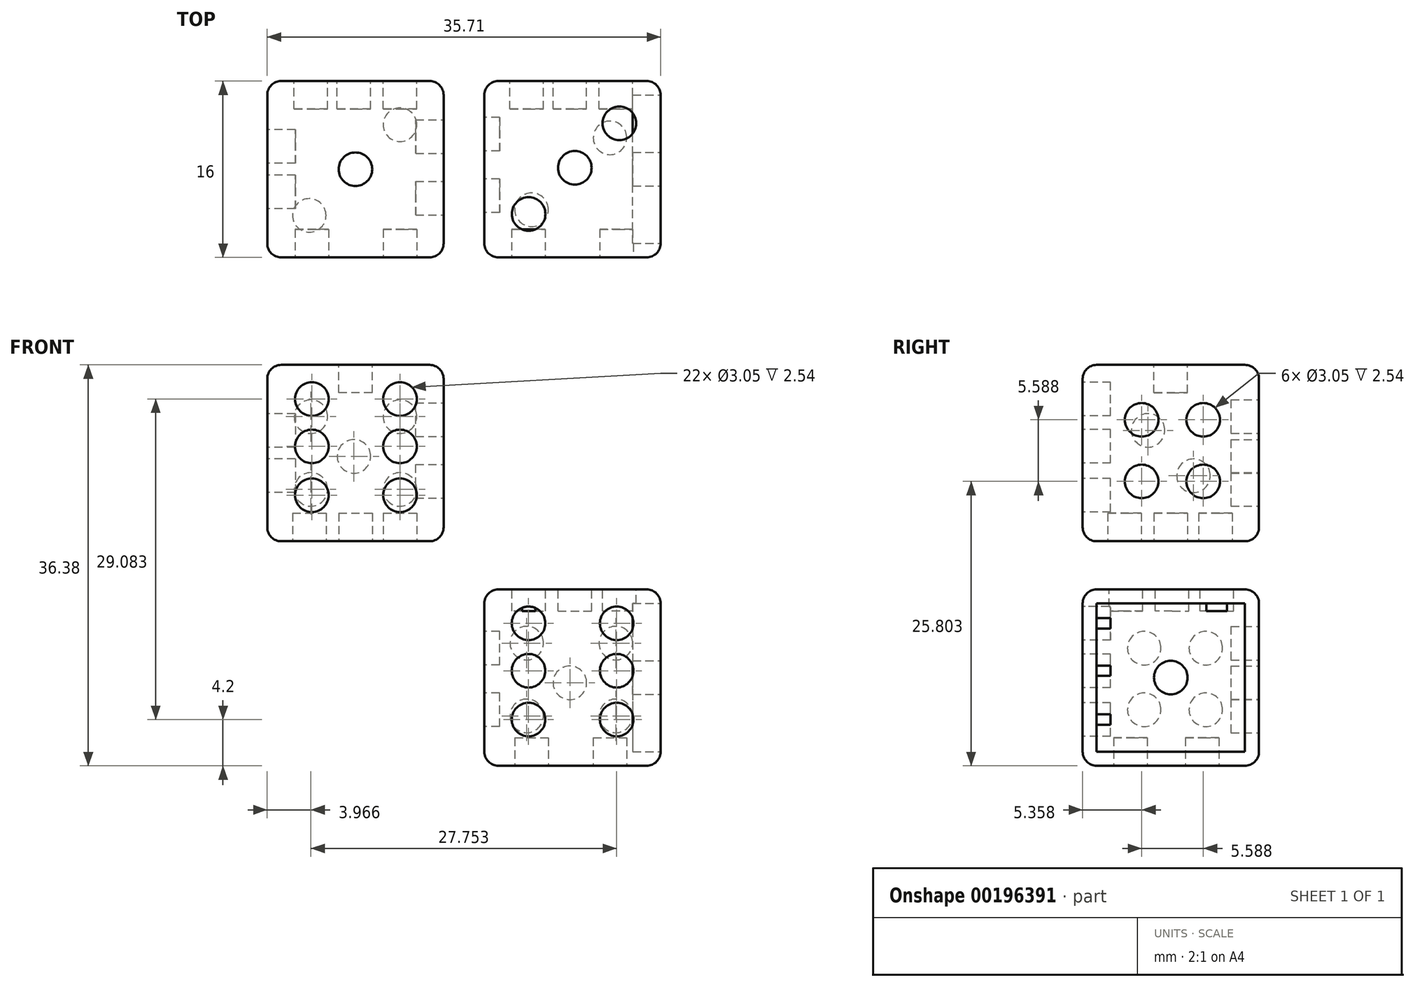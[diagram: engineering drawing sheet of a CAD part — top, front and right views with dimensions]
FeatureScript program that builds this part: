
annotation { "Feature Type Name" : "Feature", "Feature Type Description" : "" }
export const myFeature = defineFeature(function(context is Context, id is Id, definition is map)
    precondition{}
    {
        {
            var Q0;
            Q0=qCreatedBy(makeId("Front.planeOp"),FACE);
            var sketch = newSketch(context, id + "F0", { "sketchPlane" : qUnion([Q0])});
            skLineSegment(sketch, "E0.bottom", {"start": v(-12.05, 13.49) * mm, "end": v(3.96, 13.49) * mm});
            skLineSegment(sketch, "E0.top", {"start": v(-12.05, -2.52) * mm, "end": v(3.96, -2.52) * mm});
            skLineSegment(sketch, "E0.left", {"start": v(-12.05, 13.49) * mm, "end": v(-12.05, -2.52) * mm});
            skLineSegment(sketch, "E0.right", {"start": v(3.96, 13.49) * mm, "end": v(3.96, -2.52) * mm});
            skLineSegment(sketch, "E1.bottom", {"start": v(7.66, -6.89) * mm, "end": v(23.66, -6.89) * mm});
            skLineSegment(sketch, "E1.top", {"start": v(7.66, -22.89) * mm, "end": v(23.66, -22.89) * mm});
            skLineSegment(sketch, "E1.left", {"start": v(7.66, -6.89) * mm, "end": v(7.66, -22.89) * mm});
            skLineSegment(sketch, "E1.right", {"start": v(23.66, -6.89) * mm, "end": v(23.66, -22.89) * mm});
            skSolve(sketch);
        }
        {
            var Q0;
            Q0 = qSketchRegion(id + "F0", true);
            extrude(context, id + "F1", {"entities" : qUnion([Q0]), "depth" : 16 * mm});
        }
        {
            var Q0;
            Q0=makeQuery(id+"F1.opExtrude","SWEPT_EDGE",EDGE,{"disambiguationData":[OSD([sQuery(id+"F0.wireOp",EDGE,"E0.top"),sQuery(id+"F0.wireOp",EDGE,"E0.left")])]});
            var Q1;
            Q1=makeQuery(id+"F1.opExtrude","CAP_EDGE",EDGE,{"disambiguationData":[OSD([sQuery(id+"F0.wireOp",EDGE,"E0.top")])],"isStart":false});
            var Q2;
            Q2=makeQuery(id+"F1.opExtrude","CAP_EDGE",EDGE,{"disambiguationData":[OSD([sQuery(id+"F0.wireOp",EDGE,"E0.left")])],"isStart":false});
            var Q3;
            Q3=makeQuery(id+"F1.opExtrude","SWEPT_EDGE",EDGE,{"disambiguationData":[OSD([sQuery(id+"F0.wireOp",EDGE,"E0.top"),sQuery(id+"F0.wireOp",EDGE,"E0.right")])]});
            var Q4;
            Q4=makeQuery(id+"F1.opExtrude","CAP_EDGE",EDGE,{"disambiguationData":[OSD([sQuery(id+"F0.wireOp",EDGE,"E0.top")])],"isStart":true});
            var Q5;
            Q5=makeQuery(id+"F1.opExtrude","CAP_EDGE",EDGE,{"disambiguationData":[OSD([sQuery(id+"F0.wireOp",EDGE,"E0.left")])],"isStart":true});
            var Q6;
            Q6=makeQuery(id+"F1.opExtrude","CAP_EDGE",EDGE,{"disambiguationData":[OSD([sQuery(id+"F0.wireOp",EDGE,"E0.right")])],"isStart":true});
            var Q7;
            Q7=makeQuery(id+"F1.opExtrude","SWEPT_EDGE",EDGE,{"disambiguationData":[OSD([sQuery(id+"F0.wireOp",EDGE,"E0.bottom"),sQuery(id+"F0.wireOp",EDGE,"E0.right")])]});
            var Q8;
            Q8=makeQuery(id+"F1.opExtrude","CAP_EDGE",EDGE,{"disambiguationData":[OSD([sQuery(id+"F0.wireOp",EDGE,"E0.bottom")])],"isStart":false});
            var Q9;
            Q9=makeQuery(id+"F1.opExtrude","SWEPT_EDGE",EDGE,{"disambiguationData":[OSD([sQuery(id+"F0.wireOp",EDGE,"E0.bottom"),sQuery(id+"F0.wireOp",EDGE,"E0.left")])]});
            var Q10;
            Q10=makeQuery(id+"F1.opExtrude","CAP_EDGE",EDGE,{"disambiguationData":[OSD([sQuery(id+"F0.wireOp",EDGE,"E0.bottom")])],"isStart":true});
            var Q11;
            Q11=makeQuery(id+"F1.opExtrude","CAP_EDGE",EDGE,{"disambiguationData":[OSD([sQuery(id+"F0.wireOp",EDGE,"E0.right")])],"isStart":false});
            var Q12;
            Q12=makeQuery(id+"F1.opExtrude","CAP_EDGE",EDGE,{"disambiguationData":[OSD([sQuery(id+"F0.wireOp",EDGE,"E1.left")])],"isStart":false});
            var Q13;
            Q13=makeQuery(id+"F1.opExtrude","CAP_EDGE",EDGE,{"disambiguationData":[OSD([sQuery(id+"F0.wireOp",EDGE,"E1.right")])],"isStart":false});
            var Q14;
            Q14=makeQuery(id+"F1.opExtrude","CAP_EDGE",EDGE,{"disambiguationData":[OSD([sQuery(id+"F0.wireOp",EDGE,"E1.bottom")])],"isStart":false});
            var Q15;
            Q15=makeQuery(id+"F1.opExtrude","CAP_EDGE",EDGE,{"disambiguationData":[OSD([sQuery(id+"F0.wireOp",EDGE,"E1.top")])],"isStart":false});
            var Q16;
            Q16=makeQuery(id+"F1.opExtrude","SWEPT_FACE",FACE,{"disambiguationData":[OSD([sQuery(id+"F0.wireOp",EDGE,"E1.top")])]});
            var Q17;
            Q17=makeQuery(id+"F1.opExtrude","SWEPT_FACE",FACE,{"disambiguationData":[OSD([sQuery(id+"F0.wireOp",EDGE,"E1.left")])]});
            var Q18;
            Q18=makeQuery(id+"F1.opExtrude","CAP_FACE",FACE,{"disambiguationData":[OSD([sQuery(id+"F0.wireOp",EDGE,"E1.bottom"),sQuery(id+"F0.wireOp",EDGE,"E1.top"),sQuery(id+"F0.wireOp",EDGE,"E1.left"),sQuery(id+"F0.wireOp",EDGE,"E1.right")])],"isStart":true});
            var Q19;
            Q19=makeQuery(id+"F1.opExtrude","SWEPT_FACE",FACE,{"disambiguationData":[OSD([sQuery(id+"F0.wireOp",EDGE,"E1.right")])]});
            fillet(context, id + "F2", {"entities" : qUnion([Q0, Q1, Q2, Q3, Q4, Q5, Q6, Q7, Q8, Q9, Q10, Q11, Q12, Q13, Q14, Q15, Q16, Q17, Q18, Q19]), "radius" : 1.27 * mm, "tangentPropagation" : true, "allowEdgeOverflow" : false});
        }
        {
            var Q0;
            Q0=makeQuery(id+"F1.opExtrude","CAP_FACE",FACE,{"disambiguationData":[OSD([sQuery(id+"F0.wireOp",EDGE,"E0.bottom"),sQuery(id+"F0.wireOp",EDGE,"E0.top"),sQuery(id+"F0.wireOp",EDGE,"E0.left"),sQuery(id+"F0.wireOp",EDGE,"E0.right")])],"isStart":false});
            var sketch = newSketch(context, id + "F3", { "sketchPlane" : qUnion([Q0])});
            skPoint(sketch, "E2", {"position": v(-4.04, 12.22) * mm});
            skPoint(sketch, "E3", {"position": v(-4.04, -1.25) * mm});
            skPoint(sketch, "E4", {"position": v(-10.78, 5.49) * mm});
            skPoint(sketch, "E5", {"position": v(2.69, 5.49) * mm});
            skCircle(sketch, "E6", {"center": v(-8, 10.4) * mm, "radius": 1.52 * mm});
            skCircle(sketch, "E7", {"center": v(-8, 6.09) * mm, "radius": 1.52 * mm});
            skCircle(sketch, "E8", {"center": v(-8, 1.66) * mm, "radius": 1.52 * mm});
            skCircle(sketch, "E9", {"center": v(0, 10.4) * mm, "radius": 1.52 * mm});
            skCircle(sketch, "E10", {"center": v(0, 6.09) * mm, "radius": 1.52 * mm});
            skCircle(sketch, "E11", {"center": v(0, 1.66) * mm, "radius": 1.52 * mm});
            skPoint(sketch, "E12", {"position": v(15.62, -8.14) * mm});
            skPoint(sketch, "E13", {"position": v(15.62, -21.6) * mm});
            skPoint(sketch, "E14", {"position": v(8.9, -14.87) * mm});
            skPoint(sketch, "E15", {"position": v(22.36, -14.87) * mm});
            skCircle(sketch, "E16", {"center": v(11.67, -9.96) * mm, "radius": 1.52 * mm});
            skCircle(sketch, "E17", {"center": v(11.67, -14.27) * mm, "radius": 1.52 * mm});
            skCircle(sketch, "E18", {"center": v(11.67, -18.7) * mm, "radius": 1.52 * mm});
            skCircle(sketch, "E19", {"center": v(19.67, -9.96) * mm, "radius": 1.52 * mm});
            skCircle(sketch, "E20", {"center": v(19.67, -14.27) * mm, "radius": 1.52 * mm});
            skCircle(sketch, "E21", {"center": v(19.67, -18.7) * mm, "radius": 1.52 * mm});
            skSolve(sketch);
        }
        {
            var Q0;
            Q0=makeQuery(id+"F1.opExtrude","SWEPT_FACE",FACE,{"disambiguationData":[OSD([sQuery(id+"F0.wireOp",EDGE,"E0.right")])]});
            var sketch = newSketch(context, id + "F4", { "sketchPlane" : qUnion([Q0])});
            skCircle(sketch, "E22", {"center": v(-10.41, -12.22) * mm, "radius": 1.52 * mm});
            skCircle(sketch, "E23", {"center": v(-10.41, -17.8) * mm, "radius": 1.52 * mm});
            skCircle(sketch, "E24", {"center": v(-4.83, -12.22) * mm, "radius": 1.52 * mm});
            skCircle(sketch, "E25", {"center": v(-4.83, -17.8) * mm, "radius": 1.52 * mm});
            skCircle(sketch, "E26", {"center": v(-10.64, 8.5) * mm, "radius": 1.52 * mm});
            skCircle(sketch, "E27", {"center": v(-10.64, 2.91) * mm, "radius": 1.52 * mm});
            skCircle(sketch, "E28", {"center": v(-5.05, 8.5) * mm, "radius": 1.52 * mm});
            skCircle(sketch, "E29", {"center": v(-5.05, 2.91) * mm, "radius": 1.52 * mm});
            skSolve(sketch);
        }
        {
            var Q0;
            Q0=makeQuery(id+"F3.imprint","IMPRINT",FACE,{"disambiguationData":[TD([[makeQuery(id+"F3.imprint","IMPRINT",EDGE,{"derivedFrom":sQuery(id+"F3.wireOp",EDGE,"E10")}),1.0]])]});
            var Q1;
            Q1=makeQuery(id+"F3.imprint","IMPRINT",FACE,{"disambiguationData":[TD([[makeQuery(id+"F3.imprint","IMPRINT",EDGE,{"derivedFrom":sQuery(id+"F3.wireOp",EDGE,"E9")}),1.0]])]});
            var Q2;
            Q2=makeQuery(id+"F3.imprint","IMPRINT",FACE,{"disambiguationData":[TD([[makeQuery(id+"F3.imprint","IMPRINT",EDGE,{"derivedFrom":sQuery(id+"F3.wireOp",EDGE,"E6")}),1.0]])]});
            var Q3;
            Q3=makeQuery(id+"F3.imprint","IMPRINT",FACE,{"disambiguationData":[TD([[makeQuery(id+"F3.imprint","IMPRINT",EDGE,{"derivedFrom":sQuery(id+"F3.wireOp",EDGE,"E7")}),1.0]])]});
            var Q4;
            Q4=makeQuery(id+"F3.imprint","IMPRINT",FACE,{"disambiguationData":[TD([[makeQuery(id+"F3.imprint","IMPRINT",EDGE,{"derivedFrom":sQuery(id+"F3.wireOp",EDGE,"E8")}),1.0]])]});
            var Q5;
            Q5=makeQuery(id+"F3.imprint","IMPRINT",FACE,{"disambiguationData":[TD([[makeQuery(id+"F3.imprint","IMPRINT",EDGE,{"derivedFrom":sQuery(id+"F3.wireOp",EDGE,"E11")}),1.0]])]});
            extrude(context, id + "F5", {"entities" : qUnion([Q0, Q1, Q2, Q3, Q4, Q5]), "operationType" : NewBodyOperationType.REMOVE, "oppositeDirection" : true, "depth" : 2.54 * mm});
        }
        {
            var Q0;
            Q0=makeQuery(id+"F4.imprint","IMPRINT",FACE,{"disambiguationData":[TD([[makeQuery(id+"F4.imprint","IMPRINT",EDGE,{"derivedFrom":sQuery(id+"F4.wireOp",EDGE,"E22")}),1.0]])]});
            var Q1;
            Q1=makeQuery(id+"F4.imprint","IMPRINT",FACE,{"disambiguationData":[TD([[makeQuery(id+"F4.imprint","IMPRINT",EDGE,{"derivedFrom":sQuery(id+"F4.wireOp",EDGE,"E24")}),1.0]])]});
            var Q2;
            Q2=makeQuery(id+"F4.imprint","IMPRINT",FACE,{"disambiguationData":[TD([[makeQuery(id+"F4.imprint","IMPRINT",EDGE,{"derivedFrom":sQuery(id+"F4.wireOp",EDGE,"E23")}),1.0]])]});
            var Q3;
            Q3=makeQuery(id+"F4.imprint","IMPRINT",FACE,{"disambiguationData":[TD([[makeQuery(id+"F4.imprint","IMPRINT",EDGE,{"derivedFrom":sQuery(id+"F4.wireOp",EDGE,"E25")}),1.0]])]});
            extrude(context, id + "F6", {"entities" : qUnion([Q0, Q1, Q2, Q3]), "operationType" : NewBodyOperationType.REMOVE, "oppositeDirection" : true, "depth" : 3.8 * mm});
        }
        {
            var Q0;
            Q0=makeQuery(id+"F1.opExtrude","CAP_FACE",FACE,{"disambiguationData":[OSD([sQuery(id+"F0.wireOp",EDGE,"E0.bottom"),sQuery(id+"F0.wireOp",EDGE,"E0.top"),sQuery(id+"F0.wireOp",EDGE,"E0.left"),sQuery(id+"F0.wireOp",EDGE,"E0.right")])],"isStart":true});
            var sketch = newSketch(context, id + "F7", { "sketchPlane" : qUnion([Q0])});
            skCircle(sketch, "E30", {"center": v(0, 8.79) * mm, "radius": 1.52 * mm});
            skCircle(sketch, "E31", {"center": v(8.08, 8.79) * mm, "radius": 1.52 * mm});
            skCircle(sketch, "E32", {"center": v(0, 2.18) * mm, "radius": 1.52 * mm});
            skCircle(sketch, "E33", {"center": v(8.08, 2.18) * mm, "radius": 1.52 * mm});
            skCircle(sketch, "E34", {"center": v(4.18, 5.18) * mm, "radius": 1.52 * mm});
            skCircle(sketch, "E35", {"center": v(-19.6, -11.76) * mm, "radius": 1.52 * mm});
            skCircle(sketch, "E36", {"center": v(-11.5, -11.76) * mm, "radius": 1.52 * mm});
            skCircle(sketch, "E37", {"center": v(-19.6, -18.36) * mm, "radius": 1.52 * mm});
            skCircle(sketch, "E38", {"center": v(-11.5, -18.36) * mm, "radius": 1.52 * mm});
            skCircle(sketch, "E39", {"center": v(-15.42, -15.36) * mm, "radius": 1.52 * mm});
            skSolve(sketch);
        }
        {
            var Q0;
            Q0=makeQuery(id+"F7.imprint","IMPRINT",FACE,{"disambiguationData":[TD([[makeQuery(id+"F7.imprint","IMPRINT",EDGE,{"derivedFrom":sQuery(id+"F7.wireOp",EDGE,"E30")}),1.0]])]});
            var Q1;
            Q1=makeQuery(id+"F7.imprint","IMPRINT",FACE,{"disambiguationData":[TD([[makeQuery(id+"F7.imprint","IMPRINT",EDGE,{"derivedFrom":sQuery(id+"F7.wireOp",EDGE,"E34")}),1.0]])]});
            var Q2;
            Q2=makeQuery(id+"F7.imprint","IMPRINT",FACE,{"disambiguationData":[TD([[makeQuery(id+"F7.imprint","IMPRINT",EDGE,{"derivedFrom":sQuery(id+"F7.wireOp",EDGE,"E31")}),1.0]])]});
            var Q3;
            Q3=makeQuery(id+"F7.imprint","IMPRINT",FACE,{"disambiguationData":[TD([[makeQuery(id+"F7.imprint","IMPRINT",EDGE,{"derivedFrom":sQuery(id+"F7.wireOp",EDGE,"E32")}),1.0]])]});
            var Q4;
            Q4=makeQuery(id+"F7.imprint","IMPRINT",FACE,{"disambiguationData":[TD([[makeQuery(id+"F7.imprint","IMPRINT",EDGE,{"derivedFrom":sQuery(id+"F7.wireOp",EDGE,"E33")}),1.0]])]});
            extrude(context, id + "F8", {"entities" : qUnion([Q0, Q1, Q2, Q3, Q4]), "operationType" : NewBodyOperationType.REMOVE, "oppositeDirection" : true, "depth" : 2.54 * mm});
        }
        {
            var Q0;
            Q0=makeQuery(id+"F1.opExtrude","SWEPT_FACE",FACE,{"disambiguationData":[OSD([sQuery(id+"F0.wireOp",EDGE,"E0.top")])]});
            var sketch = newSketch(context, id + "F9", { "sketchPlane" : qUnion([Q0])});
            skCircle(sketch, "E40", {"center": v(-8.24, 12.2) * mm, "radius": 1.52 * mm});
            skCircle(sketch, "E41", {"center": v(-4.04, 8) * mm, "radius": 1.52 * mm});
            skCircle(sketch, "E42", {"center": v(0, 3.96) * mm, "radius": 1.52 * mm});
            skCircle(sketch, "E43", {"center": v(11.68, 12.06) * mm, "radius": 1.52 * mm});
            skCircle(sketch, "E44", {"center": v(15.87, 7.87) * mm, "radius": 1.52 * mm});
            skCircle(sketch, "E45", {"center": v(19.91, 3.83) * mm, "radius": 1.52 * mm});
            skSolve(sketch);
        }
        {
            var Q0;
            Q0=makeQuery(id+"F9.imprint","IMPRINT",FACE,{"disambiguationData":[TD([[makeQuery(id+"F9.imprint","IMPRINT",EDGE,{"derivedFrom":sQuery(id+"F9.wireOp",EDGE,"E40")}),1.0]])]});
            var Q1;
            Q1=makeQuery(id+"F9.imprint","IMPRINT",FACE,{"disambiguationData":[TD([[makeQuery(id+"F9.imprint","IMPRINT",EDGE,{"derivedFrom":sQuery(id+"F9.wireOp",EDGE,"E42")}),1.0]])]});
            var Q2;
            Q2=makeQuery(id+"F9.imprint","IMPRINT",FACE,{"disambiguationData":[TD([[makeQuery(id+"F9.imprint","IMPRINT",EDGE,{"derivedFrom":sQuery(id+"F9.wireOp",EDGE,"E41")}),1.0]])]});
            extrude(context, id + "F10", {"entities" : qUnion([Q0, Q1, Q2]), "operationType" : NewBodyOperationType.REMOVE, "oppositeDirection" : true, "depth" : 2.54 * mm});
        }
        {
            var Q0;
            Q0=makeQuery(id+"F1.opExtrude","SWEPT_FACE",FACE,{"disambiguationData":[OSD([sQuery(id+"F0.wireOp",EDGE,"E0.left")])]});
            var sketch = newSketch(context, id + "F11", { "sketchPlane" : qUnion([Q0])});
            skCircle(sketch, "E46", {"center": v(10.06, 7.55) * mm, "radius": 1.52 * mm});
            skCircle(sketch, "E47", {"center": v(5.94, 3.42) * mm, "radius": 1.52 * mm});
            skCircle(sketch, "E48", {"center": v(10.16, -12.92) * mm, "radius": 1.52 * mm});
            skCircle(sketch, "E49", {"center": v(6.03, -17.04) * mm, "radius": 1.52 * mm});
            skSolve(sketch);
        }
        {
            var Q0;
            Q0=makeQuery(id+"F11.imprint","IMPRINT",FACE,{"disambiguationData":[TD([[makeQuery(id+"F11.imprint","IMPRINT",EDGE,{"derivedFrom":sQuery(id+"F11.wireOp",EDGE,"E47")}),1.0]])]});
            var Q1;
            Q1=makeQuery(id+"F11.imprint","IMPRINT",FACE,{"disambiguationData":[TD([[makeQuery(id+"F11.imprint","IMPRINT",EDGE,{"derivedFrom":sQuery(id+"F11.wireOp",EDGE,"E46")}),1.0]])]});
            extrude(context, id + "F12", {"entities" : qUnion([Q0, Q1]), "operationType" : NewBodyOperationType.REMOVE, "oppositeDirection" : true, "depth" : 2.54 * mm});
        }
        {
            var Q0;
            Q0=makeQuery(id+"F1.opExtrude","SWEPT_FACE",FACE,{"disambiguationData":[OSD([sQuery(id+"F0.wireOp",EDGE,"E0.bottom")])]});
            var sketch = newSketch(context, id + "F13", { "sketchPlane" : qUnion([Q0])});
            skCircle(sketch, "E50", {"center": v(-4.04, -8) * mm, "radius": 1.52 * mm});
            skSolve(sketch);
        }
        {
            var Q0;
            Q0=makeQuery(id+"F13.imprint","IMPRINT",FACE,{"disambiguationData":[TD([[makeQuery(id+"F13.imprint","IMPRINT",EDGE,{"derivedFrom":sQuery(id+"F13.wireOp",EDGE,"E50")}),1.0]])]});
            extrude(context, id + "F14", {"entities" : qUnion([Q0]), "operationType" : NewBodyOperationType.REMOVE, "oppositeDirection" : true, "depth" : 2.54 * mm});
        }
        {
            var Q0;
            Q0=makeQuery(id+"F4.imprint","IMPRINT",FACE,{"disambiguationData":[TD([[makeQuery(id+"F4.imprint","IMPRINT",EDGE,{"derivedFrom":sQuery(id+"F4.wireOp",EDGE,"E26")}),1.0]])]});
            var Q1;
            Q1=makeQuery(id+"F4.imprint","IMPRINT",FACE,{"disambiguationData":[TD([[makeQuery(id+"F4.imprint","IMPRINT",EDGE,{"derivedFrom":sQuery(id+"F4.wireOp",EDGE,"E27")}),1.0]])]});
            var Q2;
            Q2=makeQuery(id+"F4.imprint","IMPRINT",FACE,{"disambiguationData":[TD([[makeQuery(id+"F4.imprint","IMPRINT",EDGE,{"derivedFrom":sQuery(id+"F4.wireOp",EDGE,"E29")}),1.0]])]});
            var Q3;
            Q3=makeQuery(id+"F4.imprint","IMPRINT",FACE,{"disambiguationData":[TD([[makeQuery(id+"F4.imprint","IMPRINT",EDGE,{"derivedFrom":sQuery(id+"F4.wireOp",EDGE,"E28")}),1.0]])]});
            extrude(context, id + "F15", {"entities" : qUnion([Q0, Q1, Q2, Q3]), "operationType" : NewBodyOperationType.REMOVE, "oppositeDirection" : true, "depth" : 2.54 * mm});
        }
        {
            var Q0;
            Q0=makeQuery(id+"F4.imprint","IMPRINT",FACE,{"disambiguationData":[TD([[makeQuery(id+"F4.imprint","IMPRINT",EDGE,{"derivedFrom":sQuery(id+"F4.wireOp",EDGE,"E25")}),1.0]])]});
            var Q1;
            Q1=makeQuery(id+"F4.imprint","IMPRINT",FACE,{"disambiguationData":[TD([[makeQuery(id+"F4.imprint","IMPRINT",EDGE,{"derivedFrom":sQuery(id+"F4.wireOp",EDGE,"E24")}),1.0]])]});
            var Q2;
            Q2=makeQuery(id+"F4.imprint","IMPRINT",FACE,{"disambiguationData":[TD([[makeQuery(id+"F4.imprint","IMPRINT",EDGE,{"derivedFrom":sQuery(id+"F4.wireOp",EDGE,"E22")}),1.0]])]});
            var Q3;
            Q3=makeQuery(id+"F4.imprint","IMPRINT",FACE,{"disambiguationData":[TD([[makeQuery(id+"F4.imprint","IMPRINT",EDGE,{"derivedFrom":sQuery(id+"F4.wireOp",EDGE,"E23")}),1.0]])]});
            extrude(context, id + "F16", {"entities" : qUnion([Q0, Q1, Q2, Q3]), "operationType" : NewBodyOperationType.REMOVE, "depth" : 5.08 * mm});
        }
        {
            var Q0;
            Q0=makeQuery(id+"F7.imprint","IMPRINT",FACE,{"disambiguationData":[TD([[makeQuery(id+"F7.imprint","IMPRINT",EDGE,{"derivedFrom":sQuery(id+"F7.wireOp",EDGE,"E35")}),1.0]])]});
            var Q1;
            Q1=makeQuery(id+"F7.imprint","IMPRINT",FACE,{"disambiguationData":[TD([[makeQuery(id+"F7.imprint","IMPRINT",EDGE,{"derivedFrom":sQuery(id+"F7.wireOp",EDGE,"E39")}),1.0]])]});
            var Q2;
            Q2=makeQuery(id+"F7.imprint","IMPRINT",FACE,{"disambiguationData":[TD([[makeQuery(id+"F7.imprint","IMPRINT",EDGE,{"derivedFrom":sQuery(id+"F7.wireOp",EDGE,"E36")}),1.0]])]});
            var Q3;
            Q3=makeQuery(id+"F7.imprint","IMPRINT",FACE,{"disambiguationData":[TD([[makeQuery(id+"F7.imprint","IMPRINT",EDGE,{"derivedFrom":sQuery(id+"F7.wireOp",EDGE,"E37")}),1.0]])]});
            var Q4;
            Q4=makeQuery(id+"F7.imprint","IMPRINT",FACE,{"disambiguationData":[TD([[makeQuery(id+"F7.imprint","IMPRINT",EDGE,{"derivedFrom":sQuery(id+"F7.wireOp",EDGE,"E38")}),1.0]])]});
            extrude(context, id + "F17", {"entities" : qUnion([Q0, Q1, Q2, Q3, Q4]), "operationType" : NewBodyOperationType.REMOVE, "oppositeDirection" : true, "depth" : 2.54 * mm});
        }
        {
            var Q0;
            Q0=makeQuery(id+"F9.imprint","IMPRINT",FACE,{"disambiguationData":[TD([[makeQuery(id+"F9.imprint","IMPRINT",EDGE,{"derivedFrom":sQuery(id+"F9.wireOp",EDGE,"E43")}),1.0]])]});
            var Q1;
            Q1=makeQuery(id+"F9.imprint","IMPRINT",FACE,{"disambiguationData":[TD([[makeQuery(id+"F9.imprint","IMPRINT",EDGE,{"derivedFrom":sQuery(id+"F9.wireOp",EDGE,"E44")}),1.0]])]});
            var Q2;
            Q2=makeQuery(id+"F9.imprint","IMPRINT",FACE,{"disambiguationData":[TD([[makeQuery(id+"F9.imprint","IMPRINT",EDGE,{"derivedFrom":sQuery(id+"F9.wireOp",EDGE,"E45")}),1.0]])]});
            var Q3;
            Q3=sQuery(id+"F9.wireOp",EDGE,"E44");
            var Q4;
            Q4=sQuery(id+"F9.wireOp",EDGE,"E45");
            var Q5;
            Q5=sQuery(id+"F9.wireOp",EDGE,"E43");
            extrude(context, id + "F18", {"entities" : qUnion([Q0, Q1, Q2]), "operationType" : NewBodyOperationType.REMOVE, "surfaceEntities" : qUnion([Q3, Q4, Q5]), "depth" : 6.35 * mm});
        }
        {
            var Q0;
            Q0=makeQuery(id+"F3.imprint","IMPRINT",FACE,{"disambiguationData":[TD([[makeQuery(id+"F3.imprint","IMPRINT",EDGE,{"derivedFrom":sQuery(id+"F3.wireOp",EDGE,"E16")}),1.0]])]});
            var Q1;
            Q1=makeQuery(id+"F3.imprint","IMPRINT",FACE,{"disambiguationData":[TD([[makeQuery(id+"F3.imprint","IMPRINT",EDGE,{"derivedFrom":sQuery(id+"F3.wireOp",EDGE,"E17")}),1.0]])]});
            var Q2;
            Q2=makeQuery(id+"F3.imprint","IMPRINT",FACE,{"disambiguationData":[TD([[makeQuery(id+"F3.imprint","IMPRINT",EDGE,{"derivedFrom":sQuery(id+"F3.wireOp",EDGE,"E19")}),1.0]])]});
            var Q3;
            Q3=makeQuery(id+"F3.imprint","IMPRINT",FACE,{"disambiguationData":[TD([[makeQuery(id+"F3.imprint","IMPRINT",EDGE,{"derivedFrom":sQuery(id+"F3.wireOp",EDGE,"E20")}),1.0]])]});
            var Q4;
            Q4=makeQuery(id+"F3.imprint","IMPRINT",FACE,{"disambiguationData":[TD([[makeQuery(id+"F3.imprint","IMPRINT",EDGE,{"derivedFrom":sQuery(id+"F3.wireOp",EDGE,"E21")}),1.0]])]});
            var Q5;
            Q5=makeQuery(id+"F3.imprint","IMPRINT",FACE,{"disambiguationData":[TD([[makeQuery(id+"F3.imprint","IMPRINT",EDGE,{"derivedFrom":sQuery(id+"F3.wireOp",EDGE,"E18")}),1.0]])]});
            extrude(context, id + "F19", {"entities" : qUnion([Q0, Q1, Q2, Q3, Q4, Q5]), "operationType" : NewBodyOperationType.REMOVE, "oppositeDirection" : true, "depth" : 2.54 * mm});
        }
        {
            var Q0;
            Q0=makeQuery(id+"F1.opExtrude","SWEPT_FACE",FACE,{"disambiguationData":[OSD([sQuery(id+"F0.wireOp",EDGE,"E1.top")])]});
            var sketch = newSketch(context, id + "F20", { "sketchPlane" : qUnion([Q0])});
            skCircle(sketch, "E51", {"center": v(11.95, 11.67) * mm, "radius": 1.52 * mm});
            skCircle(sketch, "E52", {"center": v(19.07, 5.15) * mm, "radius": 1.52 * mm});
            skSolve(sketch);
        }
        {
            var Q0;
            Q0 = qSketchRegion(id + "F20", true);
            extrude(context, id + "F21", {"entities" : qUnion([Q0]), "operationType" : NewBodyOperationType.REMOVE, "oppositeDirection" : true, "depth" : 2.54 * mm});
        }
        {
            var Q0;
            Q0=makeQuery(id+"F1.opExtrude","SWEPT_FACE",FACE,{"disambiguationData":[OSD([sQuery(id+"F0.wireOp",EDGE,"E1.right")])]});
            var sketch = newSketch(context, id + "F22", { "sketchPlane" : qUnion([Q0])});
            skLineSegment(sketch, "E53", {"start": v(-14.73, -14.89) * mm, "end": v(-1.27, -14.89) * mm});
            skCircle(sketch, "E54", {"center": v(-8, -14.89) * mm, "radius": 1.52 * mm});
            skSolve(sketch);
        }
        {
            var Q0;
            {var subQ0=sQuery(id+"F22.wireOp",EDGE,"E54");var subQ1=sQuery(id+"F22.wireOp",EDGE,"E53");var subQ2=makeQuery(id+"F22.imprint","INTERSECT",VERTEX,{"disambiguationData":[OD(0.0)],"derivedFrom":[subQ1,subQ0]});Q0=makeQuery(id+"F22.imprint","IMPRINT",FACE,{"disambiguationData":[TD([[makeQuery(id+"F22.imprint","IMPRINT",EDGE,{"disambiguationData":[TD([[subQ2,-1.0]])],"derivedFrom":subQ1}),1.0]])]});}
            var Q1;
            {var subQ0=sQuery(id+"F22.wireOp",EDGE,"E54");var subQ1=sQuery(id+"F22.wireOp",EDGE,"E53");var subQ2=makeQuery(id+"F22.imprint","INTERSECT",VERTEX,{"disambiguationData":[OD(0.0)],"derivedFrom":[subQ1,subQ0]});Q1=makeQuery(id+"F22.imprint","IMPRINT",FACE,{"disambiguationData":[TD([[makeQuery(id+"F22.imprint","IMPRINT",EDGE,{"disambiguationData":[TD([[subQ2,-1.0]])],"derivedFrom":subQ1}),-1.0]])]});}
            extrude(context, id + "F23", {"entities" : qUnion([Q0, Q1]), "operationType" : NewBodyOperationType.REMOVE, "oppositeDirection" : true, "depth" : 2.54 * mm});
        }
    });
